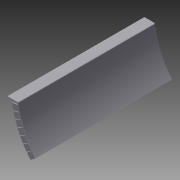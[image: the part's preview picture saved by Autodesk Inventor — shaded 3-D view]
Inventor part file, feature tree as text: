
AUTODESK INVENTOR PART (.ipt)
format: ipt  version: 2012 (Build 160160000, 160)  size: 187,392 bytes
history: native  units: in
note: dims shown in document units (in); Inventor stores cm internally (conversion verified against a paired STEP export)
features: extrude x4, sketch x2, fillet x1
ambient origin geometry x8: Origin, YZ Plane, XZ Plane, XY Plane, X Axis, Y Axis, Z Axis, Center Point
bodies: Solid1 (feature_tree)
feature tree (7):
  extrude  "Extrusion1"  Depth=0.875in
  fillet  "Fillet1"  Radius=6.886in
  sketch  "Sketch2"  dims[d3=1.0in d4=1.5in d5=0.0625in d6=11.75in d7=0.0in d8=0.0625in d16=0.5in d17=0.125in d18=2.7559in d20=0.178in d22=11.75in d23=0.0in d24=11.6875in d25=0.0in d26=0.0625in d27=0.0in]
  extrude  "Extrusion2"  Depth=1.5in
  extrude  "Extrusion3"  Depth=0.0625in
  extrude  "Extrusion4"  Depth=11.75in TaperAngle=0.0deg
  sketch  "Sketch1"  dims[d0=0.0625in d1=0.875in d2=6.886in]
